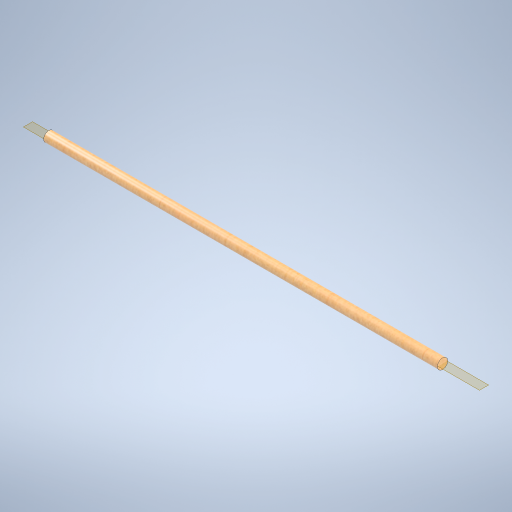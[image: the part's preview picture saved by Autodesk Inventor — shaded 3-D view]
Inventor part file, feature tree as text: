
AUTODESK INVENTOR PART (.ipt)
format: ipt  version: 2023 (Build 270158000, 158)  size: 259,072 bytes
history: native  units: mm
features: extrude x1, plane x1, sketch x1
ambient origin geometry x8: Origin, YZ Plane, XZ Plane, XY Plane, X Axis, Y Axis, Z Axis, Center Point
bodies: Volumenkörper1 (feature_tree)
feature tree (3):
  extrude  "Extrusion1"  Depth=380.0mm TaperAngle=0.0deg
  plane  "Arbeitsebene1"
  sketch  "Skizze1"  dims[d0=10.0mm d1=380.0mm d2=0.0mm d3=0.0mm]
